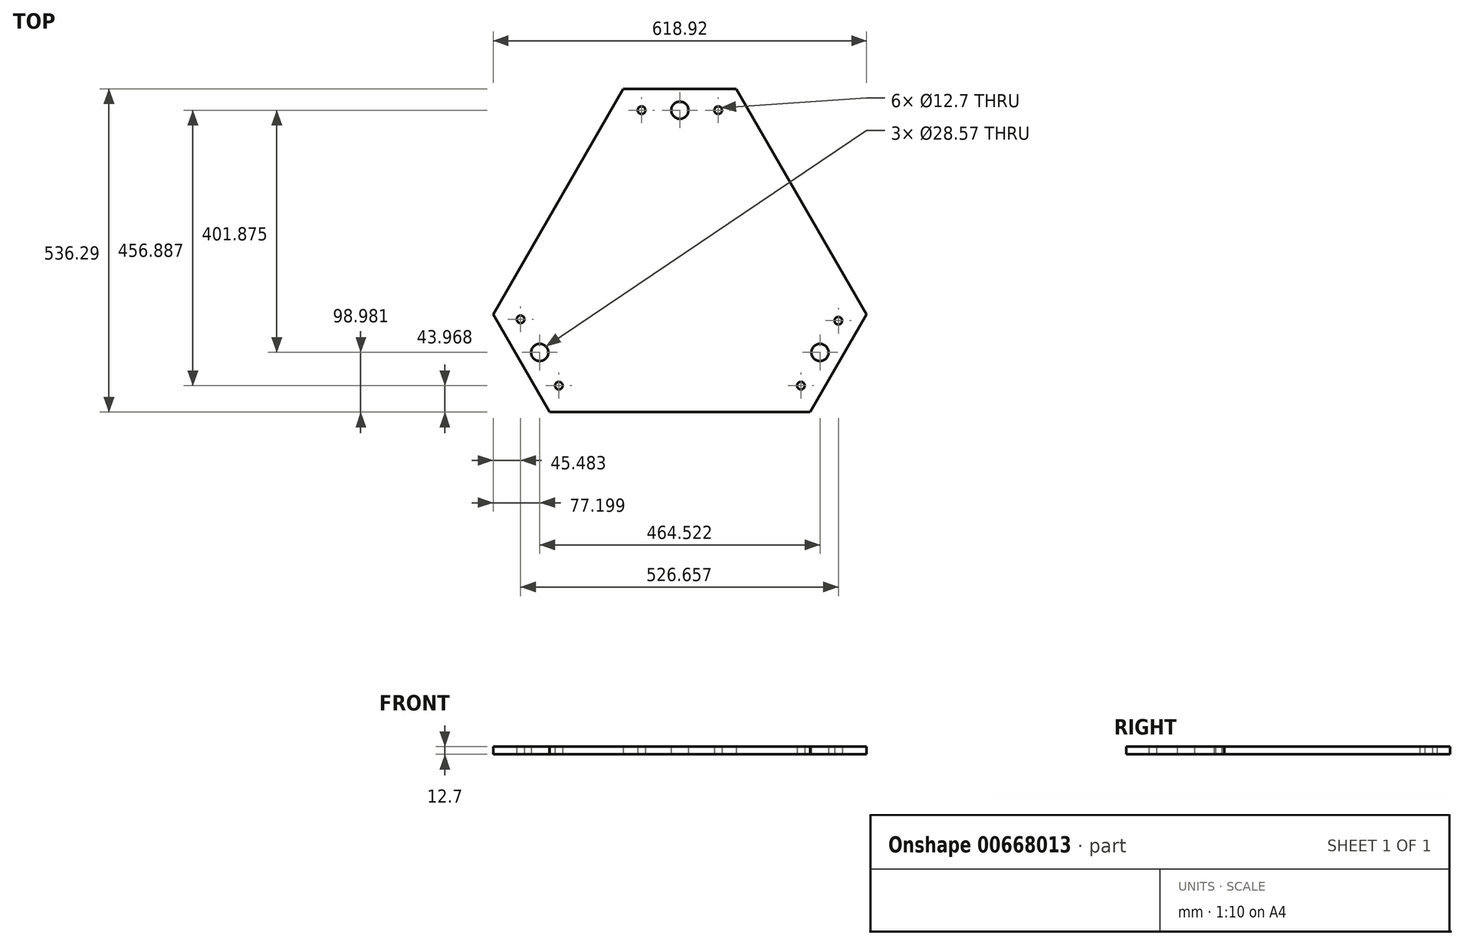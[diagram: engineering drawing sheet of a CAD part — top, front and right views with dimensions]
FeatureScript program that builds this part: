
annotation { "Feature Type Name" : "Feature", "Feature Type Description" : "" }
export const myFeature = defineFeature(function(context is Context, id is Id, definition is map)
    precondition{}
    {
        {
            var Q0;
            Q0=qCreatedBy(makeId("Top.planeOp"),FACE);
            var sketch = newSketch(context, id + "F0", { "sketchPlane" : qUnion([Q0])});
            skLineSegment(sketch, "E0", {"start": v(-273.5, -377.91) * mm, "end": v(158.3, -377.91) * mm});
            skLineSegment(sketch, "E1", {"start": v(-151.25, 158.38) * mm, "end": v(36.07, 158.38) * mm});
            skLineSegment(sketch, "E2", {"start": v(36.07, 158.38) * mm, "end": v(251.87, -215.62) * mm});
            skLineSegment(sketch, "E3", {"start": v(251.87, -215.62) * mm, "end": v(158.3, -377.91) * mm});
            skLineSegment(sketch, "E4", {"start": v(-151.25, 158.38) * mm, "end": v(-367.05, -215.62) * mm});
            skLineSegment(sketch, "E5", {"start": v(-367.05, -215.62) * mm, "end": v(-273.5, -377.91) * mm});
            skCircle(sketch, "E6", {"center": v(-57.6, 122.95) * mm, "radius": 14.29 * mm});
            skCircle(sketch, "E7", {"center": v(174.67, -278.93) * mm, "radius": 14.29 * mm});
            skCircle(sketch, "E8", {"center": v(-289.85, -278.93) * mm, "radius": 14.29 * mm});
            skCircle(sketch, "E9", {"center": v(5.9, 122.95) * mm, "radius": 6.35 * mm});
            skCircle(sketch, "E10", {"center": v(-121.1, 122.95) * mm, "radius": 6.35 * mm});
            skCircle(sketch, "E11", {"center": v(205.09, -226.17) * mm, "radius": 6.35 * mm});
            skCircle(sketch, "E12", {"center": v(142.96, -333.94) * mm, "radius": 6.35 * mm});
            skCircle(sketch, "E13", {"center": v(-321.57, -223.92) * mm, "radius": 6.35 * mm});
            skCircle(sketch, "E14", {"center": v(-258.14, -333.94) * mm, "radius": 6.35 * mm});
            skSolve(sketch);
        }
        {
            var Q0;
            Q0=makeQuery(id+"F0.imprint","IMPRINT",FACE,{"disambiguationData":[TD([[makeQuery(id+"F0.imprint","IMPRINT",EDGE,{"derivedFrom":sQuery(id+"F0.wireOp",EDGE,"E0")}),1.0]])]});
            extrude(context, id + "F1", {"entities" : qUnion([Q0]), "depth" : 12.7 * mm, "offsetDistance" : 25.4 * mm});
        }
    });
